annotation { "Feature Type Name" : "Feature", "Feature Type Description" : "" }
export const myFeature = defineFeature(function(context is Context, id is Id, definition is map)
    precondition{}
    {
        {
            var Q0;
            Q0=qCreatedBy(makeId("Front.planeOp"),FACE);
            var sketch = newSketch(context, id + "F0", { "sketchPlane" : qUnion([Q0])});
            skCircle(sketch, "E0.cCircle", {"center": v(0, 0) * mm, "radius": 45.72 * mm, "construction": true});
            skLineSegment(sketch, "E0.0", {"start": v(39.62, 22.81) * mm, "end": v(39.57, -22.9) * mm});
            skLineSegment(sketch, "E0.1", {"start": v(39.57, -22.9) * mm, "end": v(-0.05, -45.72) * mm});
            skLineSegment(sketch, "E0.2", {"start": v(-0.05, -45.72) * mm, "end": v(-39.62, -22.81) * mm});
            skLineSegment(sketch, "E0.3", {"start": v(-39.62, -22.81) * mm, "end": v(-39.57, 22.9) * mm});
            skLineSegment(sketch, "E0.4", {"start": v(-39.57, 22.9) * mm, "end": v(0.05, 45.72) * mm});
            skLineSegment(sketch, "E0.5", {"start": v(0.05, 45.72) * mm, "end": v(39.62, 22.81) * mm});
            skSolve(sketch);
        }
        {
            var Q0;
            Q0=makeQuery(id+"F0.imprint","IMPRINT",FACE,{"disambiguationData":[TD([[makeQuery(id+"F0.imprint","IMPRINT",EDGE,{"derivedFrom":sQuery(id+"F0.wireOp",EDGE,"E0.0")}),-1.0]])]});
            extrude(context, id + "F1", {"entities" : qUnion([Q0]), "depth" : 25.4 * mm});
        }
        {
            var Q0;
            Q0=makeQuery(id+"F1.opExtrude","CAP_FACE",FACE,{"disambiguationData":[OSD([sQuery(id+"F0.wireOp",EDGE,"E0.0"),sQuery(id+"F0.wireOp",EDGE,"E0.1"),sQuery(id+"F0.wireOp",EDGE,"E0.2"),sQuery(id+"F0.wireOp",EDGE,"E0.3"),sQuery(id+"F0.wireOp",EDGE,"E0.4"),sQuery(id+"F0.wireOp",EDGE,"E0.5")])],"isStart":false});
            shell(context, id + "F2", {"entities" : qUnion([Q0]), "thickness" : 2.54 * mm});
        }
        {
            var Q0;
            Q0=makeQuery(id+"F1.opExtrude","CAP_FACE",FACE,{"disambiguationData":[OSD([sQuery(id+"F0.wireOp",EDGE,"E0.0"),sQuery(id+"F0.wireOp",EDGE,"E0.1"),sQuery(id+"F0.wireOp",EDGE,"E0.2"),sQuery(id+"F0.wireOp",EDGE,"E0.3"),sQuery(id+"F0.wireOp",EDGE,"E0.4"),sQuery(id+"F0.wireOp",EDGE,"E0.5")])],"isStart":false});
            extrude(context, id + "F3", {"entities" : qUnion([Q0]), "operationType" : NewBodyOperationType.REMOVE, "oppositeDirection" : true, "depth" : 5.08 * mm});
        }
        {
            var Q0;
            Q0=makeQuery(id+"F2.opShell","OFFSET_FACE",FACE,{"disambiguationData":[OSD([sQuery(id+"F0.wireOp",EDGE,"E0.0"),sQuery(id+"F0.wireOp",EDGE,"E0.1"),sQuery(id+"F0.wireOp",EDGE,"E0.2"),sQuery(id+"F0.wireOp",EDGE,"E0.3"),sQuery(id+"F0.wireOp",EDGE,"E0.4"),sQuery(id+"F0.wireOp",EDGE,"E0.5")])]});
            chamfer(context, id + "F4", {"entities" : qUnion([Q0]), "width" : 5.08 * mm, "tangentPropagation" : true});
        }
        {
            var Q0;
            Q0=makeQuery(id+"F2.opShell","OFFSET_FACE",FACE,{"disambiguationData":[OSD([sQuery(id+"F0.wireOp",EDGE,"E0.0"),sQuery(id+"F0.wireOp",EDGE,"E0.1"),sQuery(id+"F0.wireOp",EDGE,"E0.2"),sQuery(id+"F0.wireOp",EDGE,"E0.3"),sQuery(id+"F0.wireOp",EDGE,"E0.4"),sQuery(id+"F0.wireOp",EDGE,"E0.5")])]});
            fillet(context, id + "F5", {"entities" : qUnion([Q0]), "radius" : 5.08 * mm, "tangentPropagation" : true, "allowEdgeOverflow" : false});
        }
        {
            var Q0;
            Q0=makeQuery(id+"F1.opExtrude","SWEPT_FACE",FACE,{"disambiguationData":[OSD([sQuery(id+"F0.wireOp",EDGE,"E0.2")])]});
            var sketch = newSketch(context, id + "F6", { "sketchPlane" : qUnion([Q0])});
            skCircle(sketch, "E1.cCircle", {"center": v(0, 10.16) * mm, "radius": 5.59 * mm, "construction": true});
            skPoint(sketch, "E1.cCircle.centerSnap0", {"position": v(-22.86, 10.16) * mm});
            skLineSegment(sketch, "E1.0", {"start": v(0, 15.75) * mm, "end": v(4.84, 12.95) * mm});
            skLineSegment(sketch, "E1.1", {"start": v(4.84, 12.95) * mm, "end": v(4.84, 7.37) * mm});
            skLineSegment(sketch, "E1.2", {"start": v(4.84, 7.37) * mm, "end": v(0, 4.57) * mm});
            skLineSegment(sketch, "E1.3", {"start": v(0, 4.57) * mm, "end": v(-4.84, 7.37) * mm});
            skLineSegment(sketch, "E1.4", {"start": v(-4.84, 7.37) * mm, "end": v(-4.84, 12.95) * mm});
            skLineSegment(sketch, "E1.5", {"start": v(-4.84, 12.95) * mm, "end": v(0, 15.75) * mm});
            skSolve(sketch);
        }
        {
            var Q0;
            Q0=makeQuery(id+"F1.opExtrude","SWEPT_FACE",FACE,{"disambiguationData":[OSD([sQuery(id+"F0.wireOp",EDGE,"E0.3")])]});
            var sketch = newSketch(context, id + "F7", { "sketchPlane" : qUnion([Q0])});
            skCircle(sketch, "E2.cCircle", {"center": v(10.16, 0) * mm, "radius": 6.23 * mm, "construction": true});
            skPoint(sketch, "E2.cCircle.centerSnap0", {"position": v(10.16, 22.86) * mm});
            skLineSegment(sketch, "E2.0", {"start": v(16.39, 0) * mm, "end": v(13.27, -5.4) * mm});
            skLineSegment(sketch, "E2.1", {"start": v(13.27, -5.4) * mm, "end": v(7.05, -5.4) * mm});
            skLineSegment(sketch, "E2.2", {"start": v(7.05, -5.4) * mm, "end": v(3.93, 0) * mm});
            skLineSegment(sketch, "E2.3", {"start": v(3.93, 0) * mm, "end": v(7.05, 5.4) * mm});
            skLineSegment(sketch, "E2.4", {"start": v(7.05, 5.4) * mm, "end": v(13.27, 5.4) * mm});
            skLineSegment(sketch, "E2.5", {"start": v(13.27, 5.4) * mm, "end": v(16.39, 0) * mm});
            skSolve(sketch);
        }
        {
            var Q0;
            Q0=makeQuery(id+"F7.imprint","IMPRINT",FACE,{"disambiguationData":[TD([[makeQuery(id+"F7.imprint","IMPRINT",EDGE,{"derivedFrom":sQuery(id+"F7.wireOp",EDGE,"E2.0")}),-1.0]])]});
            extrude(context, id + "F8", {"entities" : qUnion([Q0]), "operationType" : NewBodyOperationType.REMOVE, "oppositeDirection" : true, "depth" : 72.39 * mm});
        }
        {
            var Q0;
            Q0=makeQuery(id+"F6.imprint","IMPRINT",FACE,{"disambiguationData":[TD([[makeQuery(id+"F6.imprint","IMPRINT",EDGE,{"derivedFrom":sQuery(id+"F6.wireOp",EDGE,"E1.0")}),-1.0]])]});
            extrude(context, id + "F9", {"entities" : qUnion([Q0]), "operationType" : NewBodyOperationType.REMOVE, "oppositeDirection" : true, "depth" : 92.2 * mm});
        }
        {
            var Q0;
            Q0=makeQuery(id+"F1.opExtrude","SWEPT_FACE",FACE,{"disambiguationData":[OSD([sQuery(id+"F0.wireOp",EDGE,"E0.4")])]});
            var sketch = newSketch(context, id + "F10", { "sketchPlane" : qUnion([Q0])});
            skCircle(sketch, "E3.cCircle", {"center": v(0, -10.16) * mm, "radius": 5.6 * mm, "construction": true});
            skPoint(sketch, "E3.cCircle.centerSnap0", {"position": v(22.86, -10.16) * mm});
            skLineSegment(sketch, "E3.0", {"start": v(0, -15.77) * mm, "end": v(-4.86, -12.96) * mm});
            skLineSegment(sketch, "E3.1", {"start": v(-4.86, -12.96) * mm, "end": v(-4.86, -7.36) * mm});
            skLineSegment(sketch, "E3.2", {"start": v(-4.86, -7.36) * mm, "end": v(0, -4.55) * mm});
            skLineSegment(sketch, "E3.3", {"start": v(0, -4.55) * mm, "end": v(4.86, -7.36) * mm});
            skLineSegment(sketch, "E3.4", {"start": v(4.86, -7.36) * mm, "end": v(4.86, -12.96) * mm});
            skLineSegment(sketch, "E3.5", {"start": v(4.86, -12.96) * mm, "end": v(0, -15.77) * mm});
            skSolve(sketch);
        }
        {
            var Q0;
            Q0=makeQuery(id+"F10.imprint","IMPRINT",FACE,{"disambiguationData":[TD([[makeQuery(id+"F10.imprint","IMPRINT",EDGE,{"derivedFrom":sQuery(id+"F10.wireOp",EDGE,"E3.0")}),-1.0]])]});
            extrude(context, id + "F11", {"entities" : qUnion([Q0]), "operationType" : NewBodyOperationType.REMOVE, "oppositeDirection" : true, "depth" : 87.63 * mm});
        }
        {
            var Q0;
            Q0=makeQuery(id+"F2.opShell","OFFSET_FACE",FACE,{"disambiguationData":[OSD([sQuery(id+"F0.wireOp",EDGE,"E0.0"),sQuery(id+"F0.wireOp",EDGE,"E0.1"),sQuery(id+"F0.wireOp",EDGE,"E0.2"),sQuery(id+"F0.wireOp",EDGE,"E0.3"),sQuery(id+"F0.wireOp",EDGE,"E0.4"),sQuery(id+"F0.wireOp",EDGE,"E0.5")])]});
            var sketch = newSketch(context, id + "F12", { "sketchPlane" : qUnion([Q0])});
            skText(sketch, "E4", { "text": "Antonio J. Pucci\n", "fontName": "OpenSans-Regular.ttf"});
            const initialGuessF12  = {"E4": [-0.02247, -0.00209, 1, 0, 0.00454]};
            skSetInitialGuess(sketch, initialGuessF12);
            skSolve(sketch);
        }
        {
            var Q0;
            Q0 = qSketchRegion(id + "F12", true);
            extrude(context, id + "F13", {"entities" : qUnion([Q0]), "operationType" : NewBodyOperationType.ADD, "depth" : 2.18 * mm});
        }
    });